# Revit family: Reece_Grab Rail_Wolfen_Support Arm_Stainless Steel
name_source: partatom
category: Plumbing Fixtures
revit_build: Autodesk Revit 2018 (Build: 20170223_1515(x64)
units: mm (PartAtom-declared; Revit-internal decimal feet)

## family parameters
Always vertical = Yes
Cut with Voids When Loaded = Yes
Part Type = Normal
Room Calculation Point = No
Round Connector Dimension = Use Diameter
Shared = No
Work Plane-Based = Yes

## types (1)
- Stainless Steel
    Default Elevation = 0 mm  [stored 0 ft]
    Description = Wolfen Wall Mounted Support Arm Stainless Steel
    Disclaimer = THIS FILE IS THE PROPERTY OF THE REECE GROUP. IT MAY NOT BE REPRODUCED, REVERSE-ENGINEERED OR MODIFIED. ANY REPUBLICATION, TRANSMISSION OR DISTRIBUTION FOR THE PURPOSE OF COMMERCIALLY EXPLOITING THE FILES IS PROHIBITED.
    Keynote = Product #2260106, Reece_Grab Rail_Wolfen_Support Arm_Stainless Steel - Stainless Steel
    Manufacturer = Wolfen
    Model = -
    Reece_Accessory_Projection = 814 mm  [stored 2.6706 ft]
    Reece_Arm_Folded = No
    Reece_Detail_Disclaimer = THIS FILE IS THE PROPERTY OF THE REECE GROUP. IT MAY NOT BE REPRODUCED, REVERSE-ENGINEERED OR MODIFIED. ANY REPUBLICATION, TRANSMISSION OR DISTRIBUTION FOR THE PURPOSE OF COMMERCIALLY EXPLOITING THE FILES IS PROHIBITED.
    Reece_Material_Main = Reece_Brass_Brushed Stainless Steel
    Reece_Overall_Height = 144 mm  [stored 0.472441 ft]
    Reece_Overall_Length = 800 mm  [stored 2.62467 ft]
    Reece_Overall_Width = 80 mm  [stored 0.262467 ft]
    Reece_Product_Brand = Wolfen
    Reece_Product_Description = Wolfen Wall Mounted Support Arm Stainless Steel
    Reece_Product_Mount = Wall Mounted
    Reece_Product_Number = 2260106
    Reece_Product_Sub Brand = -
    Reece_Product_Type = Grab Rail
    Reece_Product_Web Page = https://www.reece.com.au
    Type Comments = Grab Rail
    URL = https://www.reece.com.au

note: [stored X ft] marks values corroborated as IEEE doubles in the binary element streams (Revit-internal decimal feet)

## geometry (parser evidence)
native form markers: Sweep x5
no freeform markers — native parametric forms only
